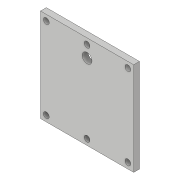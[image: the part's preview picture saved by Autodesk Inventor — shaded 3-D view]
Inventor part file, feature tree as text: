
AUTODESK INVENTOR PART (.ipt)
format: ipt  version: 2019 (Build 230136000, 136)  size: 118,784 bytes
history: native  units: mm
features: extrude x4, sketch x4
ambient origin geometry x8: Origin, YZ Plane, XZ Plane, XY Plane, X Axis, Y Axis, Z Axis, Center Point
bodies: Solid1 (feature_tree)
feature tree (8):
  extrude  "Extrusion1"  Depth=160.0mm
  extrude  "Extrusion2"  Depth=10.0mm
  extrude  "Extrusion3"  Depth=150.0mm
  extrude  "Extrusion4"  Depth=10.0mm
  sketch  "Sketch1"  dims[d0=160.0mm d1=160.0mm]
  sketch  "Sketch2"  dims[d2=10.0mm d3=0.0mm d4=10.0mm]
  sketch  "Sketch3"  dims[d5=150.0mm d6=150.0mm]
  sketch  "Sketch4"  dims[d7=150.0mm d8=150.0mm d9=150.0mm d10=10.0mm d11=150.0mm d12=10.0mm d13=10.0mm d14=10.0mm d15=10.0mm d16=10.0mm d17=0.0mm d18=0.0mm d19=80.0mm d20=10.0mm d21=140.0mm d22=10.0mm d23=10.0mm d24=0.0mm d25=0.0mm d26=80.0mm d27=30.0mm d28=17.0mm d29=0.0mm d30=0.0mm]
